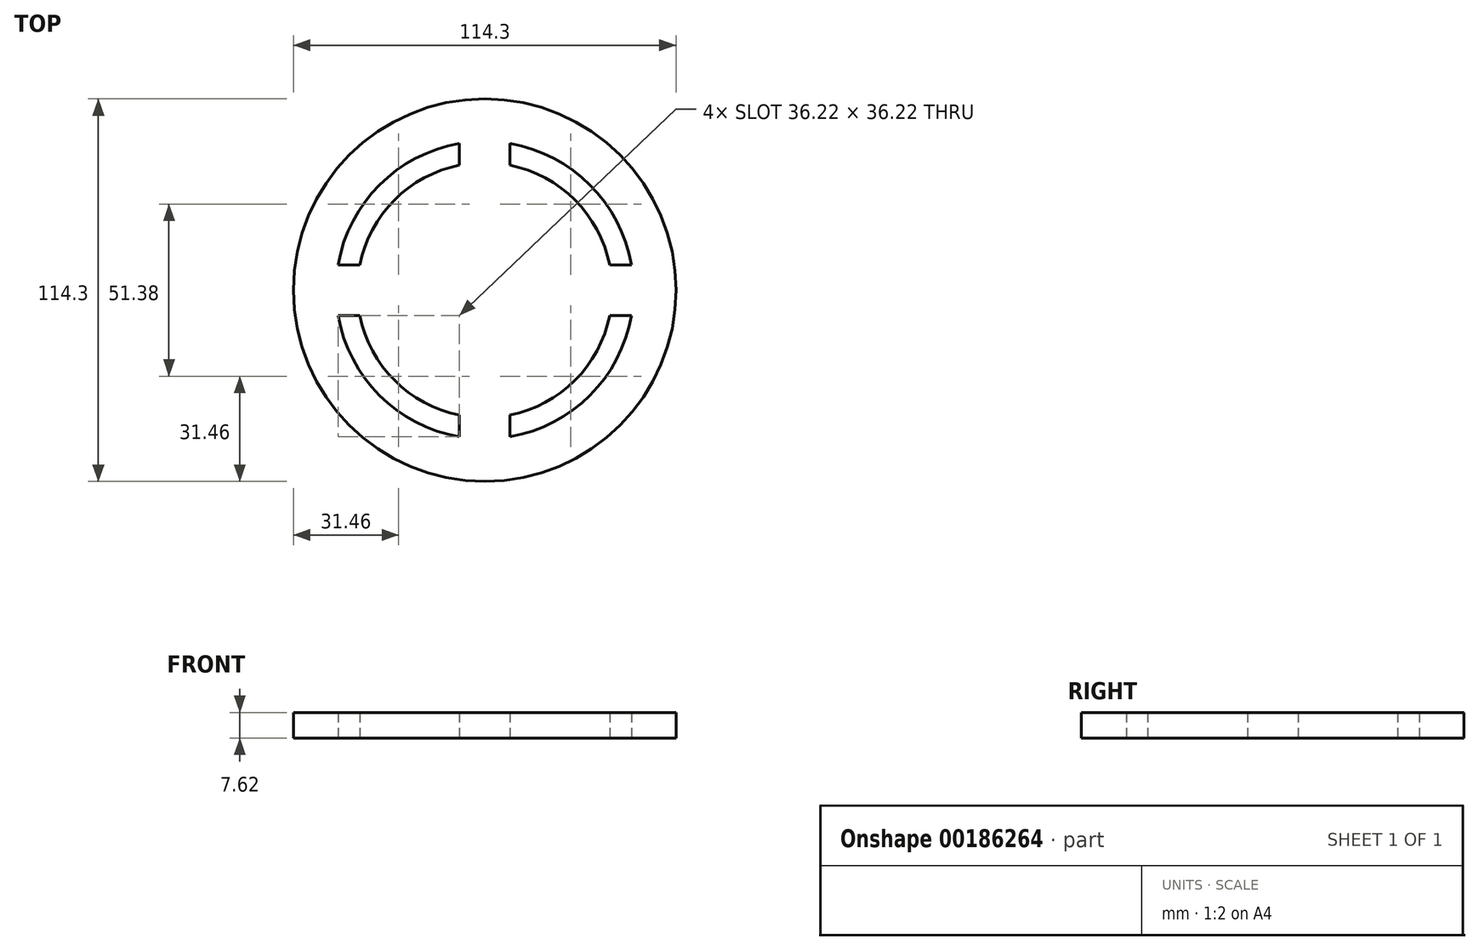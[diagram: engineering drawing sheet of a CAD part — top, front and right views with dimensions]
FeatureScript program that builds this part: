
annotation { "Feature Type Name" : "Feature", "Feature Type Description" : "" }
export const myFeature = defineFeature(function(context is Context, id is Id, definition is map)
    precondition{}
    {
        {
            var Q0;
            Q0=qCreatedBy(makeId("Top.planeOp"),FACE);
            var sketch = newSketch(context, id + "F0", { "sketchPlane" : qUnion([Q0])});
            skCircle(sketch, "E0", {"center": v(0, 0) * mm, "radius": 38.1 * mm});
            skCircle(sketch, "E1", {"center": v(0, 0) * mm, "radius": 44.45 * mm});
            skCircle(sketch, "E2", {"center": v(0, 0) * mm, "radius": 57.15 * mm});
            skPoint(sketch, "E3", {"position": v(0, 38.1) * mm});
            skPoint(sketch, "E4", {"position": v(38.1, 0) * mm});
            skPoint(sketch, "E5", {"position": v(0, -38.1) * mm});
            skPoint(sketch, "E6", {"position": v(-38.1, 0) * mm});
            skPoint(sketch, "E7", {"position": v(-44.45, 0) * mm});
            skPoint(sketch, "E8", {"position": v(0, 44.45) * mm});
            skPoint(sketch, "E9", {"position": v(44.45, 0) * mm});
            skPoint(sketch, "E10", {"position": v(0, -44.45) * mm});
            skPoint(sketch, "E11", {"position": v(-37.34, 7.58) * mm});
            skPoint(sketch, "E12", {"position": v(-37.34, -7.58) * mm});
            skPoint(sketch, "E13", {"position": v(-43.8, 7.58) * mm});
            skPoint(sketch, "E14", {"position": v(-43.8, -7.58) * mm});
            skPoint(sketch, "E15", {"position": v(7.58, 37.34) * mm});
            skPoint(sketch, "E16", {"position": v(-7.58, 37.34) * mm});
            skPoint(sketch, "E17", {"position": v(7.58, 43.8) * mm});
            skPoint(sketch, "E18", {"position": v(-7.58, 43.8) * mm});
            skPoint(sketch, "E19", {"position": v(37.34, 7.58) * mm});
            skPoint(sketch, "E20", {"position": v(37.34, -7.58) * mm});
            skPoint(sketch, "E21", {"position": v(43.8, 7.58) * mm});
            skPoint(sketch, "E22", {"position": v(43.8, -7.58) * mm});
            skPoint(sketch, "E23", {"position": v(7.58, -37.34) * mm});
            skPoint(sketch, "E24", {"position": v(-7.58, -37.34) * mm});
            skPoint(sketch, "E25", {"position": v(-7.58, -43.8) * mm});
            skPoint(sketch, "E26", {"position": v(7.58, -43.8) * mm});
            skArc(sketch, "E27", {"start": v(-37.34, 7.58) * mm, "mid": v(-38.1, 0) * mm, "end": v(-37.34, -7.58) * mm});
            skArc(sketch, "E28", {"start": v(-43.8, 7.58) * mm, "mid": v(-44.45, 0) * mm, "end": v(-43.8, -7.58) * mm});
            skArc(sketch, "E29", {"start": v(7.58, 37.34) * mm, "mid": v(0, 38.1) * mm, "end": v(-7.58, 37.34) * mm});
            skArc(sketch, "E30", {"start": v(7.58, 43.8) * mm, "mid": v(0, 44.45) * mm, "end": v(-7.58, 43.8) * mm});
            skArc(sketch, "E31", {"start": v(37.34, -7.58) * mm, "mid": v(38.1, 0) * mm, "end": v(37.34, 7.58) * mm});
            skArc(sketch, "E32", {"start": v(43.8, -7.58) * mm, "mid": v(44.45, 0) * mm, "end": v(43.8, 7.58) * mm});
            skArc(sketch, "E33", {"start": v(-7.58, -37.34) * mm, "mid": v(0, -38.1) * mm, "end": v(7.58, -37.34) * mm});
            skArc(sketch, "E34", {"start": v(-7.58, -43.8) * mm, "mid": v(0, -44.45) * mm, "end": v(7.58, -43.8) * mm});
            skLineSegment(sketch, "E35", {"start": v(-37.34, 7.58) * mm, "end": v(-43.8, 7.58) * mm});
            skLineSegment(sketch, "E36", {"start": v(-37.34, -7.58) * mm, "end": v(-43.8, -7.58) * mm});
            skLineSegment(sketch, "E37", {"start": v(-7.58, 43.8) * mm, "end": v(-7.58, 37.34) * mm});
            skLineSegment(sketch, "E38", {"start": v(7.58, 37.34) * mm, "end": v(7.58, 43.8) * mm});
            skLineSegment(sketch, "E39", {"start": v(37.34, 7.58) * mm, "end": v(43.8, 7.58) * mm});
            skLineSegment(sketch, "E40", {"start": v(37.34, -7.58) * mm, "end": v(43.8, -7.58) * mm});
            skLineSegment(sketch, "E41", {"start": v(7.58, -37.34) * mm, "end": v(7.58, -43.8) * mm});
            skLineSegment(sketch, "E42", {"start": v(-7.58, -37.34) * mm, "end": v(-7.58, -43.8) * mm});
            skSolve(sketch);
        }
        {
            var Q0;
            Q0 = qSketchRegion(id + "F0", true);
            var Q1;
            {var subQ0=sQuery(id+"F0.wireOp",EDGE,"E0");var subQ4=makeQuery(id+"F0.imprint","INTERSECT",VERTEX,{"derivedFrom":[subQ0,sQuery(id+"F0.wireOp",EDGE,"E38")]});Q1=makeQuery(id+"F0.imprint","IMPRINT",FACE,{"disambiguationData":[TD([[makeQuery(id+"F0.imprint","IMPRINT",EDGE,{"disambiguationData":[TD([[subQ4,1.0]])],"derivedFrom":subQ0}),1.0]])]});}
            var Q2;
            {var subQ0=sQuery(id+"F0.wireOp",EDGE,"E37");Q2=makeQuery(id+"F0.imprint","IMPRINT",FACE,{"disambiguationData":[TD([[makeQuery(id+"F0.imprint","IMPRINT",EDGE,{"derivedFrom":subQ0}),1.0]])]});}
            var Q3;
            {var subQ0=sQuery(id+"F0.wireOp",EDGE,"E39");Q3=makeQuery(id+"F0.imprint","IMPRINT",FACE,{"disambiguationData":[TD([[makeQuery(id+"F0.imprint","IMPRINT",EDGE,{"derivedFrom":subQ0}),-1.0]])]});}
            var Q4;
            {var subQ0=sQuery(id+"F0.wireOp",EDGE,"E41");Q4=makeQuery(id+"F0.imprint","IMPRINT",FACE,{"disambiguationData":[TD([[makeQuery(id+"F0.imprint","IMPRINT",EDGE,{"derivedFrom":subQ0}),-1.0]])]});}
            var Q5;
            {var subQ0=sQuery(id+"F0.wireOp",EDGE,"E35");Q5=makeQuery(id+"F0.imprint","IMPRINT",FACE,{"disambiguationData":[TD([[makeQuery(id+"F0.imprint","IMPRINT",EDGE,{"derivedFrom":subQ0}),1.0]])]});}
            extrude(context, id + "F1", {"entities" : qUnion([Q0, Q1, Q2, Q3, Q4, Q5]), "depth" : 7.62 * mm});
        }
    });
